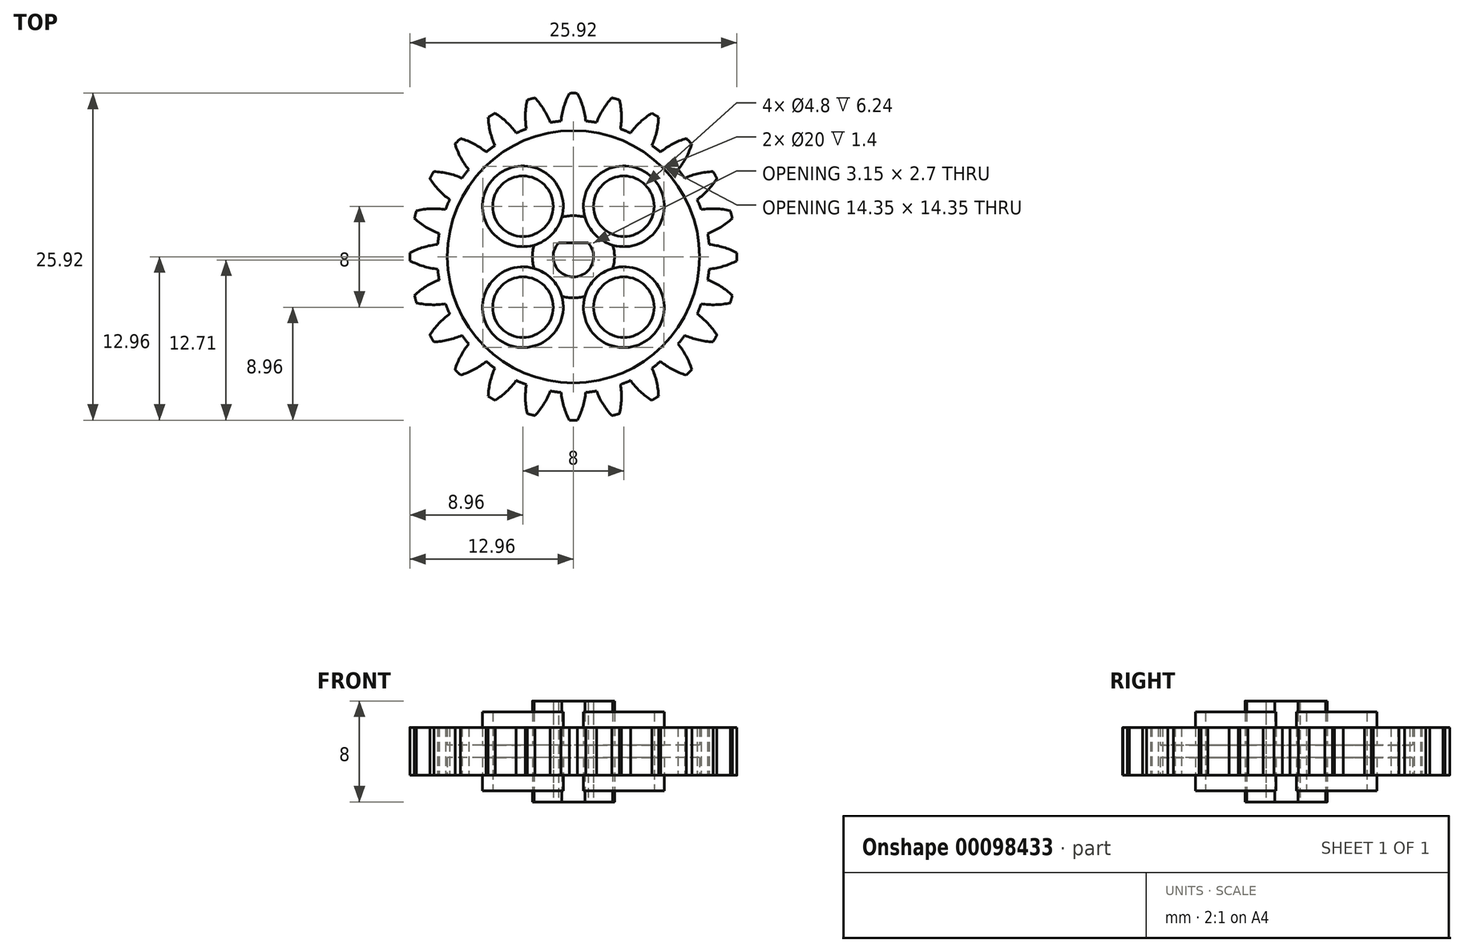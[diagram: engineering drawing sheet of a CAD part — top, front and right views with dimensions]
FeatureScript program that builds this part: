
annotation { "Feature Type Name" : "Feature", "Feature Type Description" : "" }
export const myFeature = defineFeature(function(context is Context, id is Id, definition is map)
    precondition{}
    {
        {
            var Q0;
            Q0=qCreatedBy(makeId("Top.planeOp"),FACE);
            var sketch = newSketch(context, id + "F0", { "sketchPlane" : qUnion([Q0])});
            skArc(sketch, "E0", {"start": v(-1.16, 1.1) * mm, "mid": v(0, -1.6) * mm, "end": v(1.16, 1.1) * mm});
            skCircle(sketch, "E1", {"center": v(-4, 4) * mm, "radius": 2.4 * mm});
            skCircle(sketch, "E2", {"center": v(-4, 4) * mm, "radius": 3.2 * mm});
            skCircle(sketch, "E3", {"center": v(0, 0) * mm, "radius": 10 * mm});
            skCircle(sketch, "E4.1.0", {"center": v(-4, -4) * mm, "radius": 2.4 * mm});
            skCircle(sketch, "E4.1.1", {"center": v(-4, -4) * mm, "radius": 3.2 * mm});
            skCircle(sketch, "E4.2.0", {"center": v(4, -4) * mm, "radius": 2.4 * mm});
            skCircle(sketch, "E4.2.1", {"center": v(4, -4) * mm, "radius": 3.2 * mm});
            skCircle(sketch, "E4.3.0", {"center": v(4, 4) * mm, "radius": 2.4 * mm});
            skCircle(sketch, "E4.3.1", {"center": v(4, 4) * mm, "radius": 3.2 * mm});
            skArc(sketch, "E5", {"start": v(0.31, 12.96) * mm, "mid": v(0, 12.96) * mm, "end": v(-0.31, 12.96) * mm});
            skCircle(sketch, "E6", {"center": v(0, 0) * mm, "radius": 10.8 * mm});
            skArc(sketch, "E7.trimOffspring", {"start": v(0.98, 10.76) * mm, "mid": v(0.75, 11.89) * mm, "end": v(0.31, 12.96) * mm});
            skArc(sketch, "E8.trimOffspring", {"start": v(-0.98, 10.76) * mm, "mid": v(-0.75, 11.89) * mm, "end": v(-0.31, 12.96) * mm});
            skLineSegment(sketch, "E9", {"start": v(-1.16, 1.1) * mm, "end": v(1.16, 1.1) * mm});
            skArc(sketch, "E10", {"start": v(-3.12, 0.92) * mm, "mid": v(-3.26, 0) * mm, "end": v(-3.12, -0.92) * mm});
            skArc(sketch, "E11.trimOffspring", {"start": v(0.92, 3.12) * mm, "mid": v(0, 3.26) * mm, "end": v(-0.92, 3.12) * mm});
            skArc(sketch, "E12.trimOffspring", {"start": v(3.12, -0.92) * mm, "mid": v(3.26, 0) * mm, "end": v(3.12, 0.92) * mm});
            skArc(sketch, "E13.trimOffspring", {"start": v(-0.92, -3.12) * mm, "mid": v(0, -3.26) * mm, "end": v(0.92, -3.12) * mm});
            skSolve(sketch);
        }
        {
            var Q0;
            Q0=makeQuery(id+"F0.imprint","IMPRINT",FACE,{"disambiguationData":[TD([[makeQuery(id+"F0.imprint","IMPRINT",EDGE,{"derivedFrom":sQuery(id+"F0.wireOp",EDGE,"E1")}),-1.0]])]});
            var Q1;
            Q1=makeQuery(id+"F0.imprint","IMPRINT",FACE,{"disambiguationData":[TD([[makeQuery(id+"F0.imprint","IMPRINT",EDGE,{"derivedFrom":sQuery(id+"F0.wireOp",EDGE,"E4.3.0")}),-1.0]])]});
            var Q2;
            Q2=makeQuery(id+"F0.imprint","IMPRINT",FACE,{"disambiguationData":[TD([[makeQuery(id+"F0.imprint","IMPRINT",EDGE,{"derivedFrom":sQuery(id+"F0.wireOp",EDGE,"E4.2.0")}),-1.0]])]});
            var Q3;
            Q3=makeQuery(id+"F0.imprint","IMPRINT",FACE,{"disambiguationData":[TD([[makeQuery(id+"F0.imprint","IMPRINT",EDGE,{"derivedFrom":sQuery(id+"F0.wireOp",EDGE,"E4.1.0")}),-1.0]])]});
            extrude(context, id + "F1", {"entities" : qUnion([Q0, Q1, Q2, Q3]), "endBound" : BoundingType.SYMMETRIC, "depth" : 6.24 * mm});
        }
        {
            var Q0;
            Q0=makeQuery(id+"F0.imprint","IMPRINT",FACE,{"disambiguationData":[TD([[makeQuery(id+"F0.imprint","IMPRINT",EDGE,{"derivedFrom":sQuery(id+"F0.wireOp",EDGE,"E0")}),-1.0]])]});
            extrude(context, id + "F2", {"entities" : qUnion([Q0]), "operationType" : NewBodyOperationType.ADD, "endBound" : BoundingType.SYMMETRIC, "depth" : 8 * mm});
        }
        {
            var Q0;
            Q0=makeQuery(id+"F0.imprint","IMPRINT",FACE,{"disambiguationData":[TD([[makeQuery(id+"F0.imprint","IMPRINT",EDGE,{"derivedFrom":sQuery(id+"F0.wireOp",EDGE,"E3")}),1.0]])]});
            extrude(context, id + "F3", {"entities" : qUnion([Q0]), "operationType" : NewBodyOperationType.ADD, "endBound" : BoundingType.SYMMETRIC, "depth" : 1 * mm});
        }
        {
            var Q0;
            Q0=makeQuery(id+"F0.imprint","IMPRINT",FACE,{"disambiguationData":[TD([[makeQuery(id+"F0.imprint","IMPRINT",EDGE,{"derivedFrom":sQuery(id+"F0.wireOp",EDGE,"E3")}),-1.0]])]});
            extrude(context, id + "F4", {"entities" : qUnion([Q0]), "operationType" : NewBodyOperationType.ADD, "endBound" : BoundingType.SYMMETRIC, "depth" : 3.8 * mm});
        }
        {
            var Q0;
            Q0=makeQuery(id+"F0.imprint","IMPRINT",FACE,{"disambiguationData":[TD([[makeQuery(id+"F0.imprint","IMPRINT",EDGE,{"derivedFrom":sQuery(id+"F0.wireOp",EDGE,"E5")}),1.0]])]});
            var Q1;
            Q1=sQuery(id+"F0.wireOp",EDGE,"E6");
            extrude(context, id + "F5", {"entities" : qUnion([Q0]), "surfaceEntities" : qUnion([Q1]), "endBound" : BoundingType.SYMMETRIC, "depth" : 3.8 * mm});
        }
        {
            var Q0;
            Q0=makeQuery(id+"F5.opExtrude","SWEPT_BODY",BODY,{"disambiguationData":[OSD([sQuery(id+"F0.wireOp",EDGE,"E5"),sQuery(id+"F0.wireOp",EDGE,"E6"),sQuery(id+"F0.wireOp",EDGE,"E7.trimOffspring"),sQuery(id+"F0.wireOp",EDGE,"E8.trimOffspring")])]});
            var Q1;
            Q1=makeQuery(id+"F2.opExtrude","SWEPT_FACE",FACE,{"disambiguationData":[OSD([sQuery(id+"F0.wireOp",EDGE,"E0")])]});
            circularPattern(context, id + "F6", {"operationType" : NewBodyOperationType.ADD, "entities" : qUnion([Q0]), "axis" : qUnion([Q1]), "angle" : 360 * degree, "instanceCount" : 24, "equalSpace" : true});
        }
    });
